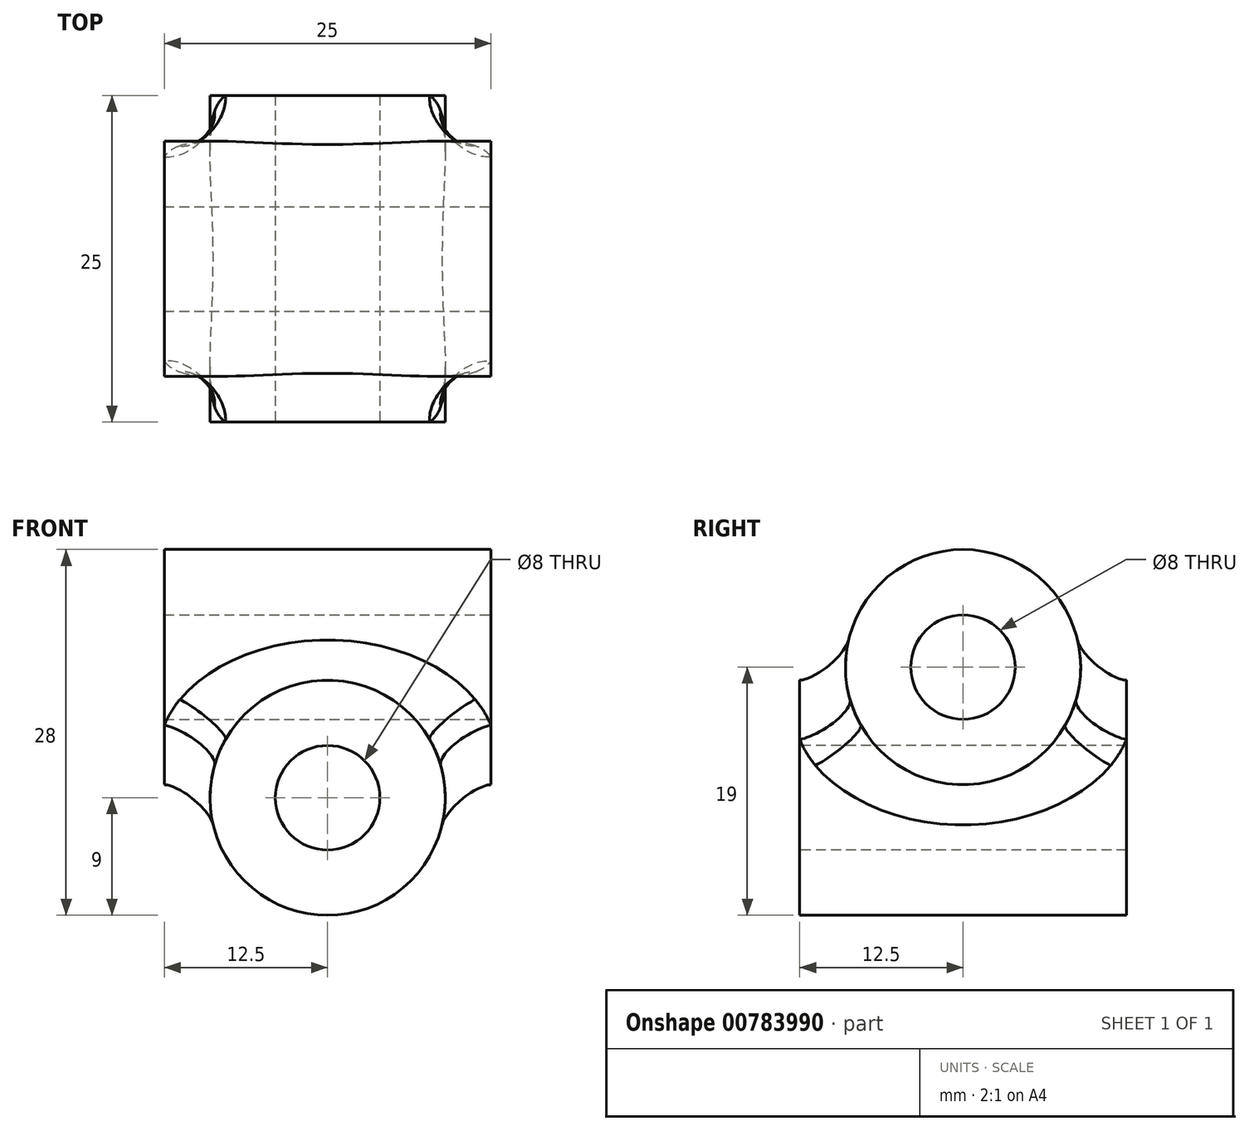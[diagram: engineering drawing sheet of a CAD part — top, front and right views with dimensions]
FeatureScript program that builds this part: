
annotation { "Feature Type Name" : "Feature", "Feature Type Description" : "" }
export const myFeature = defineFeature(function(context is Context, id is Id, definition is map)
    precondition{}
    {
        {
            var Q0;
            Q0=qCreatedBy(makeId("Front.planeOp"),FACE);
            var sketch = newSketch(context, id + "F0", { "sketchPlane" : qUnion([Q0])});
            skCircle(sketch, "E0", {"center": v(0, 0) * mm, "radius": 9 * mm});
            skSolve(sketch);
        }
        {
            var Q0;
            Q0=qCreatedBy(makeId("Right.planeOp"),FACE);
            var sketch = newSketch(context, id + "F1", { "sketchPlane" : qUnion([Q0])});
            skCircle(sketch, "E1", {"center": v(0, 10) * mm, "radius": 9 * mm});
            skSolve(sketch);
        }
        {
            var Q0;
            Q0=makeQuery(id+"F0.imprint","IMPRINT",FACE,{"disambiguationData":[TD([[makeQuery(id+"F0.imprint","IMPRINT",EDGE,{"derivedFrom":sQuery(id+"F0.wireOp",EDGE,"E0")}),1.0]])]});
            extrude(context, id + "F2", {"entities" : qUnion([Q0]), "endBound" : BoundingType.SYMMETRIC, "depth" : 25 * mm, "offsetDistance" : 25 * mm});
        }
        {
            var Q0;
            Q0=makeQuery(id+"F1.imprint","IMPRINT",FACE,{"disambiguationData":[TD([[makeQuery(id+"F1.imprint","IMPRINT",EDGE,{"derivedFrom":sQuery(id+"F1.wireOp",EDGE,"E1")}),1.0]])]});
            extrude(context, id + "F3", {"entities" : qUnion([Q0]), "operationType" : NewBodyOperationType.ADD, "endBound" : BoundingType.SYMMETRIC, "depth" : 25 * mm, "offsetDistance" : 25 * mm});
        }
        {
            var Q0;
            Q0=makeQuery(id+"F2.opExtrude","CAP_FACE",FACE,{"disambiguationData":[OSD([sQuery(id+"F0.wireOp",EDGE,"E0")])],"isStart":false});
            var sketch = newSketch(context, id + "F4", { "sketchPlane" : qUnion([Q0])});
            skPoint(sketch, "E2", {"position": v(0, 0) * mm});
            skSolve(sketch);
        }
        {
            var Q0;
            Q0=sQuery(id+"F4.wireOp",VERTEX,"E2");
            var Q1;
            Q1=makeQuery(id+"F2.opExtrude","SWEPT_BODY",BODY,{"disambiguationData":[OSD([sQuery(id+"F0.wireOp",EDGE,"E0")])]});
            hole(context, id + "F5", {"style" : HoleStyle.SIMPLE, "endStyle" : HoleEndStyle.THROUGH, "holeDiameter" : 8 * mm, "majorDiameter" : 5 * mm, "isTappedThrough" : true, "tappedDepth" : 12 * mm, "tapClearance" : 3, "locations" : qUnion([Q0]), "scope" : qUnion([Q1])});
        }
        {
            var Q0;
            Q0=makeQuery(id+"F3.opExtrude","CAP_FACE",FACE,{"disambiguationData":[OSD([sQuery(id+"F1.wireOp",EDGE,"E1")])],"isStart":false});
            var sketch = newSketch(context, id + "F6", { "sketchPlane" : qUnion([Q0])});
            skPoint(sketch, "E3", {"position": v(0, 10) * mm});
            skSolve(sketch);
        }
        {
            var Q0;
            Q0=sQuery(id+"F6.wireOp",VERTEX,"E3");
            var Q1;
            Q1=makeQuery(id+"F2.opExtrude","SWEPT_BODY",BODY,{"disambiguationData":[OSD([sQuery(id+"F0.wireOp",EDGE,"E0")])]});
            hole(context, id + "F7", {"style" : HoleStyle.SIMPLE, "endStyle" : HoleEndStyle.THROUGH, "holeDiameter" : 8 * mm, "majorDiameter" : 5 * mm, "isTappedThrough" : true, "tappedDepth" : 12 * mm, "tapClearance" : 3, "locations" : qUnion([Q0]), "scope" : qUnion([Q1])});
        }
        {
            var Q0;
            Q0=makeQuery(id+"F3.boolean.opBoolean","INTERSECT",EDGE,{"derivedFrom":[makeQuery(id+"F2.opExtrude","SWEPT_FACE",FACE,{"disambiguationData":[OSD([sQuery(id+"F0.wireOp",EDGE,"E0")])]}),makeQuery(id+"F3.opExtrude","SWEPT_FACE",FACE,{"disambiguationData":[OSD([sQuery(id+"F1.wireOp",EDGE,"E1")])]})]});
            fillet(context, id + "F8", {"entities" : qUnion([Q0]), "radius" : 4 * mm, "tangentPropagation" : true, "rho" : 0.3, "crossSection" : FilletCrossSection.CONIC, "allowEdgeOverflow" : false});
        }
    });
